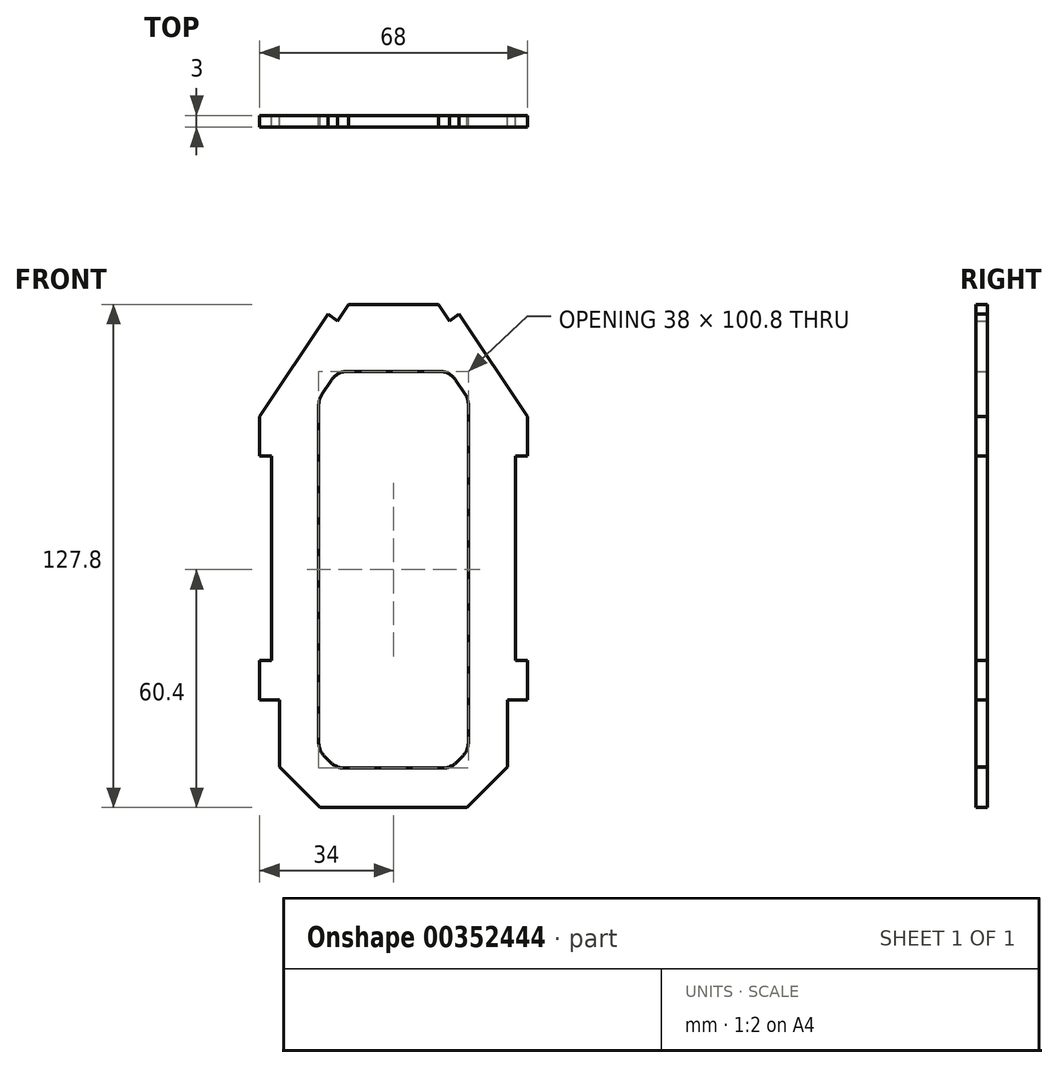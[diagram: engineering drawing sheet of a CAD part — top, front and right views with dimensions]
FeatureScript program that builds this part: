
annotation { "Feature Type Name" : "Feature", "Feature Type Description" : "" }
export const myFeature = defineFeature(function(context is Context, id is Id, definition is map)
    precondition{}
    {
        {
            var Q0;
            Q0=qCreatedBy(makeId("Front.planeOp"),FACE);
            var sketch = newSketch(context, id + "F0", { "sketchPlane" : qUnion([Q0])});
            skLineSegment(sketch, "E0.bottom", {"start": v(-11.4, 63.5) * mm, "end": v(11.4, 63.5) * mm});
            skLineSegment(sketch, "E0.top", {"start": v(-18.7, -64.3) * mm, "end": v(18.7, -64.3) * mm});
            skLineSegment(sketch, "E0.left", {"start": v(-34, 35) * mm, "end": v(-34, 25) * mm});
            skPoint(sketch, "E0.middle", {"position": v(0, -0.4) * mm});
            skPoint(sketch, "E1", {"position": v(-15, 63.5) * mm});
            skLineSegment(sketch, "E2", {"start": v(-16.66, 61) * mm, "end": v(-34, 35) * mm});
            skLineSegment(sketch, "E3", {"start": v(-11.4, 63.5) * mm, "end": v(-14.17, 59.34) * mm});
            skLineSegment(sketch, "E4", {"start": v(-14.17, 59.34) * mm, "end": v(-16.66, 61) * mm});
            skPoint(sketch, "E5.orphan", {"position": v(-34, 63.5) * mm});
            skLineSegment(sketch, "E6", {"start": v(-34, 25) * mm, "end": v(-31, 25) * mm});
            skLineSegment(sketch, "E7", {"start": v(-31, 25) * mm, "end": v(-31, -27) * mm});
            skLineSegment(sketch, "E8", {"start": v(-31, -27) * mm, "end": v(-34, -27) * mm});
            skLineSegment(sketch, "E9.trimOffspring", {"start": v(-34, -27) * mm, "end": v(-34, -37) * mm});
            skLineSegment(sketch, "E10", {"start": v(-34, -37) * mm, "end": v(-29, -37) * mm});
            skLineSegment(sketch, "E11", {"start": v(-29, -37) * mm, "end": v(-29, -54) * mm});
            skLineSegment(sketch, "E12", {"start": v(-29, -54) * mm, "end": v(-18.7, -64.3) * mm});
            skPoint(sketch, "E13.orphan", {"position": v(-34, -64.3) * mm});
            skLineSegment(sketch, "E14.MirrorCS", {"start": v(11.4, 63.5) * mm, "end": v(14.17, 59.34) * mm});
            skLineSegment(sketch, "E15.MirrorCS", {"start": v(14.17, 59.34) * mm, "end": v(16.66, 61) * mm});
            skLineSegment(sketch, "E16.MirrorCS", {"start": v(16.66, 61) * mm, "end": v(34, 35) * mm});
            skLineSegment(sketch, "E17.MirrorCS", {"start": v(34, 35) * mm, "end": v(34, 25) * mm});
            skLineSegment(sketch, "E18.MirrorCS", {"start": v(34, 25) * mm, "end": v(31, 25) * mm});
            skLineSegment(sketch, "E19.MirrorCS", {"start": v(31, 25) * mm, "end": v(31, -27) * mm});
            skLineSegment(sketch, "E20.MirrorCS", {"start": v(34, -27) * mm, "end": v(34, -37) * mm});
            skLineSegment(sketch, "E21.MirrorCS", {"start": v(29, -37) * mm, "end": v(29, -54) * mm});
            skLineSegment(sketch, "E22.MirrorCS", {"start": v(29, -54) * mm, "end": v(18.7, -64.3) * mm});
            skLineSegment(sketch, "E23", {"start": v(31, -27) * mm, "end": v(34, -27) * mm});
            skLineSegment(sketch, "E24", {"start": v(34, -37) * mm, "end": v(29, -37) * mm});
            skPoint(sketch, "E25.orphan", {"position": v(34, -64.3) * mm});
            skPoint(sketch, "E0.right.start.orphan", {"position": v(34, 63.5) * mm});
            skLineSegment(sketch, "E26.5", {"start": v(-15.8, 44.27) * mm, "end": v(-18.16, 40.73) * mm});
            skLineSegment(sketch, "E26.6", {"start": v(15.8, 44.27) * mm, "end": v(18.16, 40.73) * mm});
            skLineSegment(sketch, "E26.8", {"start": v(-19, 37.96) * mm, "end": v(-19, -47.79) * mm});
            skLineSegment(sketch, "E26.12", {"start": v(-17.54, -51.32) * mm, "end": v(-16.02, -52.84) * mm});
            skLineSegment(sketch, "E26.13", {"start": v(-12.49, -54.3) * mm, "end": v(12.49, -54.3) * mm});
            skLineSegment(sketch, "E26.14", {"start": v(17.54, -51.32) * mm, "end": v(16.02, -52.84) * mm});
            skLineSegment(sketch, "E26.15", {"start": v(19, 37.96) * mm, "end": v(19, -47.79) * mm});
            skLineSegment(sketch, "E27", {"start": v(-11.64, 46.5) * mm, "end": v(11.64, 46.5) * mm});
            skPoint(sketch, "E28.visualSharp", {"position": v(-19, -49.86) * mm});
            skArc(sketch, "E28.filletArc", {"start": v(-19, -47.79) * mm, "mid": v(-18.62, -49.7) * mm, "end": v(-17.54, -51.32) * mm});
            skPoint(sketch, "E29.visualSharp", {"position": v(-14.56, -54.3) * mm});
            skArc(sketch, "E29.filletArc", {"start": v(-16.02, -52.84) * mm, "mid": v(-14.4, -53.92) * mm, "end": v(-12.49, -54.3) * mm});
            skPoint(sketch, "E30.visualSharp", {"position": v(14.56, -54.3) * mm});
            skArc(sketch, "E30.filletArc", {"start": v(12.49, -54.3) * mm, "mid": v(14.4, -53.92) * mm, "end": v(16.02, -52.84) * mm});
            skPoint(sketch, "E31.visualSharp", {"position": v(19, -49.86) * mm});
            skArc(sketch, "E31.filletArc", {"start": v(17.54, -51.32) * mm, "mid": v(18.62, -49.7) * mm, "end": v(19, -47.79) * mm});
            skPoint(sketch, "E32.visualSharp", {"position": v(14.31, 46.5) * mm});
            skArc(sketch, "E32.filletArc", {"start": v(15.8, 44.27) * mm, "mid": v(14, 45.9) * mm, "end": v(11.64, 46.5) * mm});
            skPoint(sketch, "E33.visualSharp", {"position": v(-14.31, 46.5) * mm});
            skArc(sketch, "E33.filletArc", {"start": v(-11.64, 46.5) * mm, "mid": v(-14, 45.9) * mm, "end": v(-15.8, 44.27) * mm});
            skPoint(sketch, "E34.visualSharp", {"position": v(-19, 39.47) * mm});
            skArc(sketch, "E34.filletArc", {"start": v(-18.16, 40.73) * mm, "mid": v(-18.79, 39.4) * mm, "end": v(-19, 37.96) * mm});
            skPoint(sketch, "E35.visualSharp", {"position": v(19, 39.47) * mm});
            skArc(sketch, "E35.filletArc", {"start": v(19, 37.96) * mm, "mid": v(18.79, 39.4) * mm, "end": v(18.16, 40.73) * mm});
            skSolve(sketch);
        }
        {
            var Q0;
            Q0 = qSketchRegion(id + "F0", true);
            extrude(context, id + "F1", {"entities" : qUnion([Q0]), "depth" : 3 * mm, "symmetric" : true});
        }
    });
